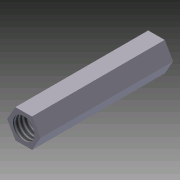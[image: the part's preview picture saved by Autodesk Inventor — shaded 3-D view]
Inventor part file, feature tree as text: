
AUTODESK INVENTOR PART (.ipt)
format: ipt  version: 2011 (Build 150239000, 239)  size: 75,264 bytes
history: native  units: in
note: dims shown in document units (in); Inventor stores cm internally (conversion verified against a paired STEP export)
features: extrude x1, thread x1, sketch x1
ambient origin geometry x8: Origin, YZ Plane, XZ Plane, XY Plane, X Axis, Y Axis, Z Axis, Center Point
bodies: Solid1 (feature_tree)
feature tree (3):
  extrude  "Extrusion1"  Depth=0.162in
  thread  "Thread1"  [1 undecoded]
  sketch  "Sketch1"  dims[d0=0.25in d1=0.162in d3=1.0in d4=0.0in d5=1.0in d6=0.0in]
note: 1 required parameter value undecoded (feature->parameter linkage not recoverable at this tier; creation-order binding heuristic only, values carry confidence <= 0.55)
